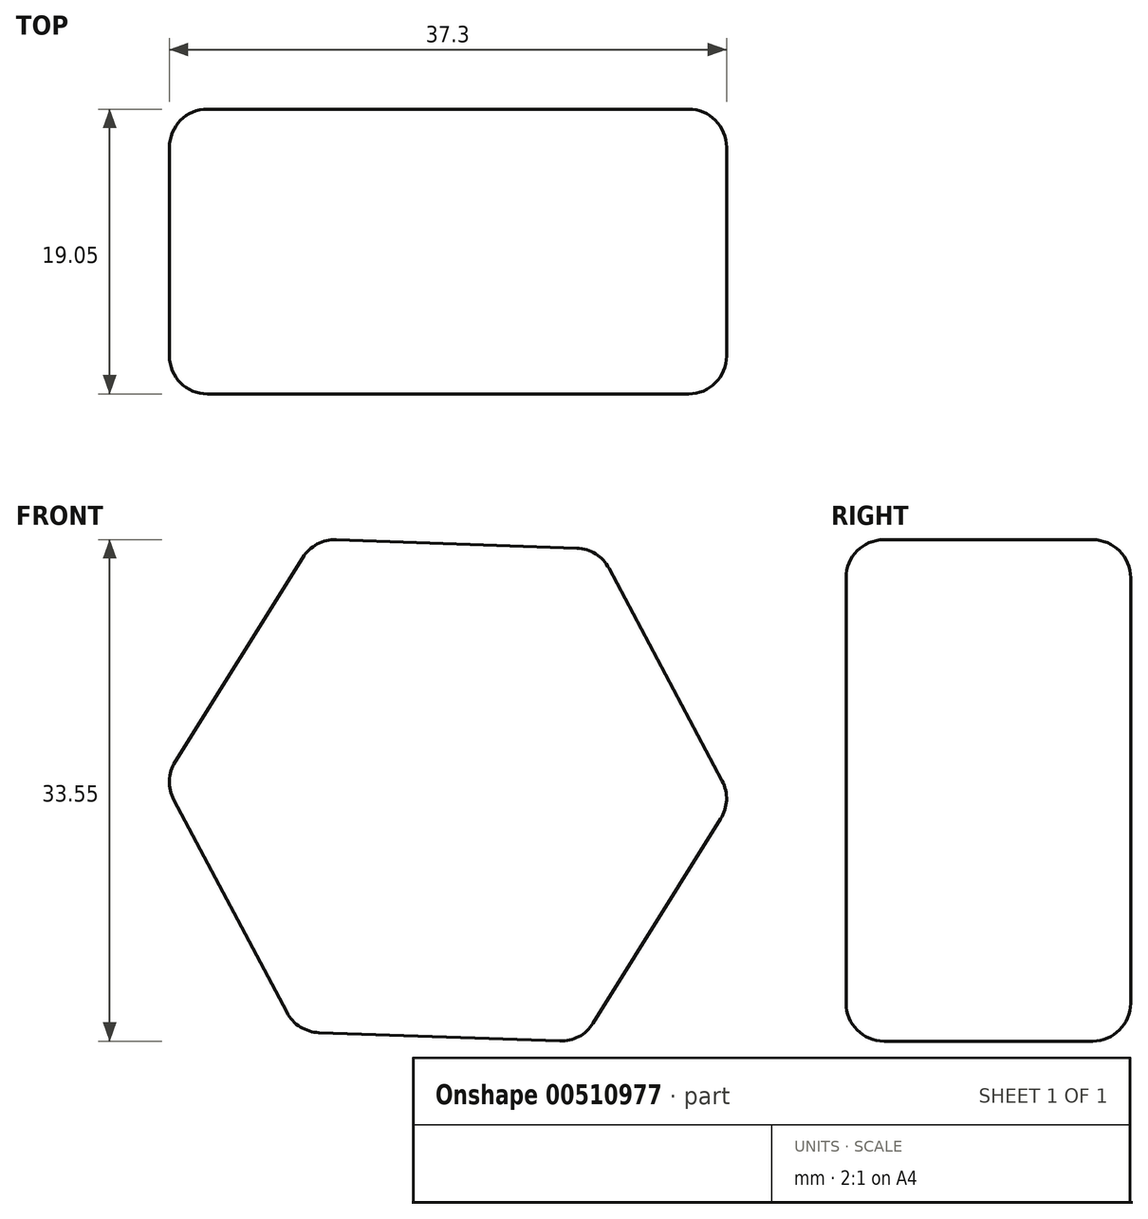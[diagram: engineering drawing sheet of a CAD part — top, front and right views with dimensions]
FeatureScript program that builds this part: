
annotation { "Feature Type Name" : "Feature", "Feature Type Description" : "" }
export const myFeature = defineFeature(function(context is Context, id is Id, definition is map)
    precondition{}
    {
        {
            var Q0;
            Q0=qCreatedBy(makeId("Front.planeOp"),FACE);
            var sketch = newSketch(context, id + "F0", { "sketchPlane" : qUnion([Q0])});
            skCircle(sketch, "E0.cCircle", {"center": v(0, 1.38) * mm, "radius": 16.5 * mm, "construction": true});
            skLineSegment(sketch, "E0.0", {"start": v(-19.04, 2.05) * mm, "end": v(-8.94, 18.2) * mm});
            skLineSegment(sketch, "E0.1", {"start": v(-8.94, 18.2) * mm, "end": v(10.1, 17.54) * mm});
            skLineSegment(sketch, "E0.2", {"start": v(10.1, 17.54) * mm, "end": v(19.04, 0.72) * mm});
            skLineSegment(sketch, "E0.3", {"start": v(19.04, 0.72) * mm, "end": v(8.94, -15.44) * mm});
            skLineSegment(sketch, "E0.4", {"start": v(8.94, -15.44) * mm, "end": v(-10.1, -14.77) * mm});
            skLineSegment(sketch, "E0.5", {"start": v(-10.1, -14.77) * mm, "end": v(-19.04, 2.05) * mm});
            skPoint(sketch, "E0.0.midPoint", {"position": v(-14, 10.13) * mm});
            skSolve(sketch);
        }
        {
            var Q0;
            Q0 = qSketchRegion(id + "F0", true);
            extrude(context, id + "F1", {"entities" : qUnion([Q0]), "depth" : 19.05 * mm});
        }
        {
            var Q0;
            Q0=makeQuery(id+"F1.opExtrude","CAP_EDGE",EDGE,{"disambiguationData":[OSD([sQuery(id+"F0.wireOp",EDGE,"E0.2")])],"isStart":false});
            var Q1;
            Q1=makeQuery(id+"F1.opExtrude","CAP_EDGE",EDGE,{"disambiguationData":[OSD([sQuery(id+"F0.wireOp",EDGE,"E0.1")])],"isStart":false});
            var Q2;
            Q2=makeQuery(id+"F1.opExtrude","SWEPT_EDGE",EDGE,{"disambiguationData":[OSD([sQuery(id+"F0.wireOp",EDGE,"E0.1"),sQuery(id+"F0.wireOp",EDGE,"E0.2")])]});
            var Q3;
            Q3=makeQuery(id+"F1.opExtrude","SWEPT_EDGE",EDGE,{"disambiguationData":[OSD([sQuery(id+"F0.wireOp",EDGE,"E0.2"),sQuery(id+"F0.wireOp",EDGE,"E0.3")])]});
            var Q4;
            Q4=makeQuery(id+"F1.opExtrude","CAP_EDGE",EDGE,{"disambiguationData":[OSD([sQuery(id+"F0.wireOp",EDGE,"E0.3")])],"isStart":false});
            var Q5;
            Q5=makeQuery(id+"F1.opExtrude","CAP_EDGE",EDGE,{"disambiguationData":[OSD([sQuery(id+"F0.wireOp",EDGE,"E0.2")])],"isStart":true});
            var Q6;
            Q6=makeQuery(id+"F1.opExtrude","CAP_EDGE",EDGE,{"disambiguationData":[OSD([sQuery(id+"F0.wireOp",EDGE,"E0.3")])],"isStart":true});
            var Q7;
            Q7=makeQuery(id+"F1.opExtrude","CAP_EDGE",EDGE,{"disambiguationData":[OSD([sQuery(id+"F0.wireOp",EDGE,"E0.1")])],"isStart":true});
            var Q8;
            Q8=makeQuery(id+"F1.opExtrude","SWEPT_EDGE",EDGE,{"disambiguationData":[OSD([sQuery(id+"F0.wireOp",EDGE,"E0.4"),sQuery(id+"F0.wireOp",EDGE,"E0.5")])]});
            var Q9;
            Q9=makeQuery(id+"F1.opExtrude","CAP_EDGE",EDGE,{"disambiguationData":[OSD([sQuery(id+"F0.wireOp",EDGE,"E0.4")])],"isStart":true});
            var Q10;
            Q10=makeQuery(id+"F1.opExtrude","CAP_EDGE",EDGE,{"disambiguationData":[OSD([sQuery(id+"F0.wireOp",EDGE,"E0.5")])],"isStart":true});
            var Q11;
            Q11=makeQuery(id+"F1.opExtrude","SWEPT_EDGE",EDGE,{"disambiguationData":[OSD([sQuery(id+"F0.wireOp",EDGE,"E0.0"),sQuery(id+"F0.wireOp",EDGE,"E0.5")])]});
            var Q12;
            Q12=makeQuery(id+"F1.opExtrude","CAP_EDGE",EDGE,{"disambiguationData":[OSD([sQuery(id+"F0.wireOp",EDGE,"E0.5")])],"isStart":false});
            var Q13;
            Q13=makeQuery(id+"F1.opExtrude","SWEPT_FACE",FACE,{"disambiguationData":[OSD([sQuery(id+"F0.wireOp",EDGE,"E0.4")])]});
            var Q14;
            Q14=makeQuery(id+"F1.opExtrude","CAP_EDGE",EDGE,{"disambiguationData":[OSD([sQuery(id+"F0.wireOp",EDGE,"E0.0")])],"isStart":false});
            var Q15;
            Q15=makeQuery(id+"F1.opExtrude","SWEPT_EDGE",EDGE,{"disambiguationData":[OSD([sQuery(id+"F0.wireOp",EDGE,"E0.0"),sQuery(id+"F0.wireOp",EDGE,"E0.1")])]});
            var Q16;
            Q16=makeQuery(id+"F1.opExtrude","CAP_EDGE",EDGE,{"disambiguationData":[OSD([sQuery(id+"F0.wireOp",EDGE,"E0.0")])],"isStart":true});
            fillet(context, id + "F2", {"entities" : qUnion([Q0, Q1, Q2, Q3, Q4, Q5, Q6, Q7, Q8, Q9, Q10, Q11, Q12, Q13, Q14, Q15, Q16]), "radius" : 2.54 * mm, "tangentPropagation" : true, "allowEdgeOverflow" : false});
        }
    });
